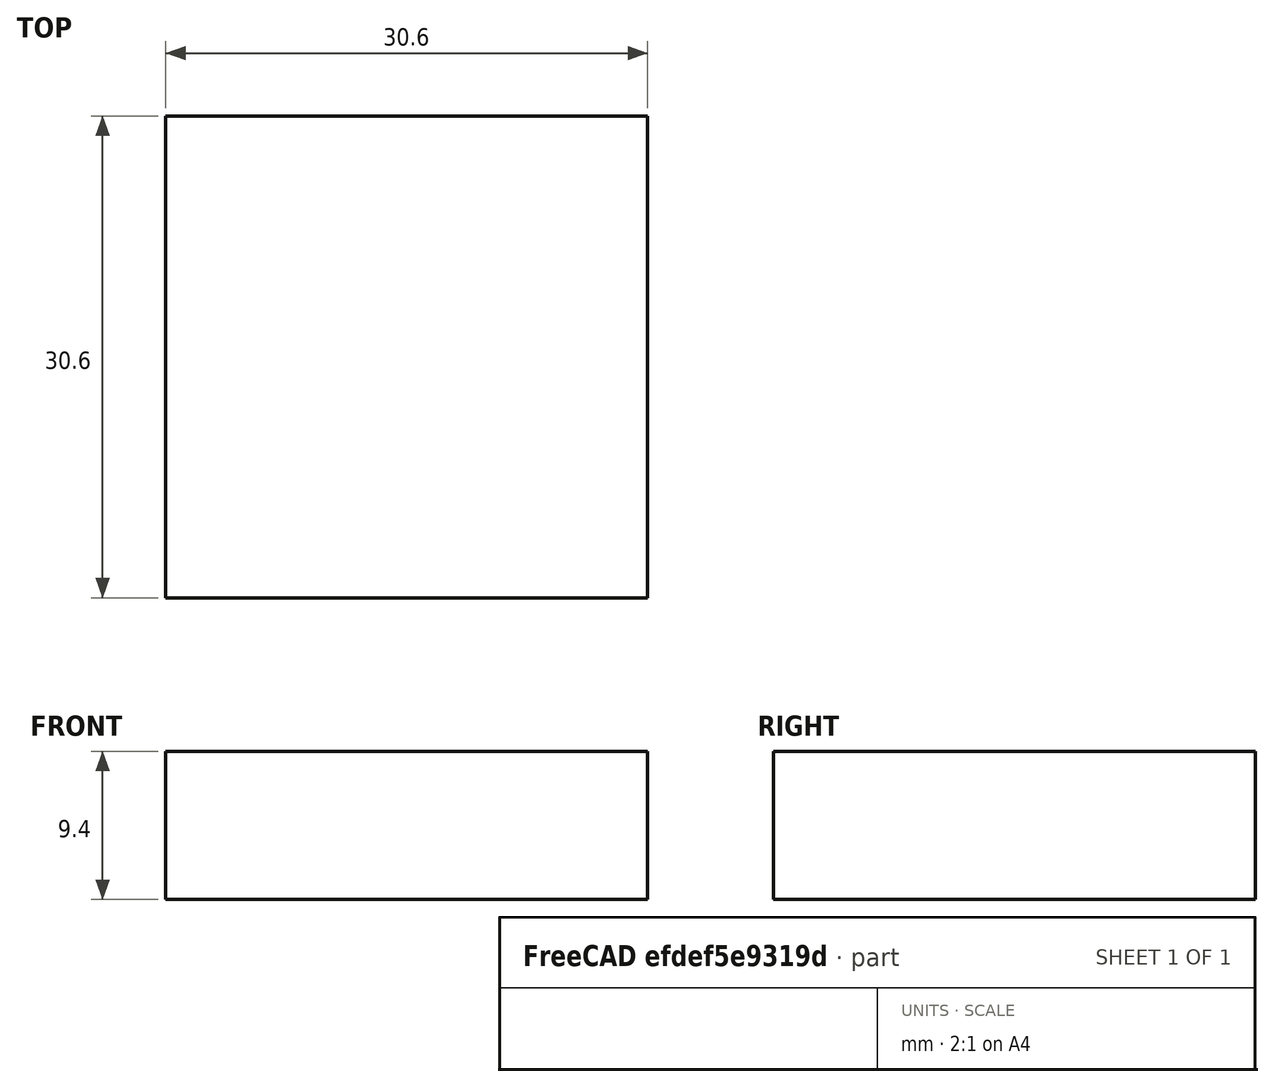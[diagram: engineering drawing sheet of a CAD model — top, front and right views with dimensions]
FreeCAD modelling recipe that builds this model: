
FCSTD DOCUMENT  (FreeCAD 0.17R13320 (Git))
Label: ring
License: All rights reserved
LicenseURL: http://en.wikipedia.org/wiki/All_rights_reserved
objects: Path::FeaturePython×7, Part::FeaturePython×2, Mesh::FeaturePython×2, Sketcher::SketchObject×1, PartDesign::Pad×1, PartDesign::Body×1, App::FeaturePython×1, Path::FeatureCompoundPython×1
note: 8 computed .brp shape members not serialized (recipe doc carries the construction recipe); baked Part::Feature solids carry a one-line shape summary decoded from their .brp

FEATURE [Sketcher::SketchObject] Sketch
  MapMode = 5
  Support = -> [XY_Plane]
  sketch-geometry (2):
    g0: Circle CenterX=0 CenterY=0 CenterZ=0 NormalX=0 NormalY=0 NormalZ=1 AngleXU=0 Radius=4.1
    g1: Circle CenterX=0 CenterY=0 CenterZ=0 NormalX=0 NormalY=0 NormalZ=1 AngleXU=0 Radius=4.9
  constraints (4):
    c: Coincident(g0,g-1)
    c: Coincident(g1,g-1)
    c: Radius(g0) = 4.1
    c: Radius(g1) = 4.9
FEATURE [PartDesign::Pad] Pad
  Length = 7
  Length2 = 100
  Profile = -> Sketch
  Type = 0
FEATURE [PartDesign::Body] Body
  Group = -> [Sketch,Pad]
  Origin = -> Origin
  Tip = -> Pad
FEATURE [App::FeaturePython] SetupSheet  # Path/CAM operation (typed FeaturePython)
  ClearanceHeightExpression = StartDepth+SetupSheet.ClearanceHeightOffset
  ClearanceHeightOffset = 5
  FinalDepthExpression = OpFinalDepth
  HorizRapid = 0
  SafeHeightExpression = StartDepth+SetupSheet.SafeHeightOffset
  SafeHeightOffset = 3
  StartDepthExpression = OpStartDepth
  StepDownExpression = OpToolDiameter
  VertRapid = 0
FEATURE [Part::FeaturePython] Clone  label="Base-Body"  # Draft clone (typed FeaturePython)
  AttacherType = Attacher::AttachEngine3D
  Fuse = false
  Objects = -> [Body]
  PathResource = Base
  Placement = pos=(14.9,14.9,-9.4) rot=(0,0,1;0rad)
  Scale = (1,1,1)
FEATURE [Path::FeaturePython] Default_Tool  label="Default Tool"  # Path/CAM operation (typed FeaturePython)
  HorizFeed = 0
  HorizRapid = 0
  SpindleDir = 0
  SpindleSpeed = 0
  ToolNumber = 1
  VertFeed = 0
  VertRapid = 0
  expr: HorizRapid = SetupSheet.HorizRapid
  expr: VertRapid = SetupSheet.VertRapid
FEATURE [Part::FeaturePython] Stock  # WARN: FeaturePython — macro-defined, semantics opaque (R4)
  Base = -> Body
  ExtXneg = 10
  ExtXpos = 10
  ExtYneg = 10
  ExtYpos = 10
  ExtZneg = 0
  ExtZpos = 2.4
  Placement = pos=(14.9,14.9,-9.4) rot=(0,0,1;0rad)
  StockType = FromBase
FEATURE [Path::FeaturePython] T3__8mm  label="T3: 8mm"  # Path/CAM operation (typed FeaturePython)
  HorizFeed = 0
  HorizRapid = 0
  SpindleDir = 0
  SpindleSpeed = 0
  ToolNumber = 3
  VertFeed = 0
  VertRapid = 0
  expr: HorizRapid = SetupSheet.HorizRapid
  expr: VertRapid = SetupSheet.VertRapid
FEATURE [Path::FeaturePython] Helix  # Path/CAM operation (typed FeaturePython)
  Active = true
  Base = -> [Clone]
  ClearanceHeight = 5
  Direction = 0
  FinalDepth = -10
  OpFinalDepth = -9.4
  OpStartDepth = 0
  OpToolDiameter = 8
  SafeHeight = 3
  StartDepth = 0
  StartSide = 0
  StepDown = 0.5
  StepOver = 30
  ToolController = -> T3__8mm
  expr: ClearanceHeight = StartDepth + SetupSheet.ClearanceHeightOffset
  expr: SafeHeight = StartDepth + SetupSheet.SafeHeightOffset
  expr: StartDepth = OpStartDepth
FEATURE [Path::FeaturePython] Contour  # Path/CAM operation (typed FeaturePython)
  Active = true
  AreaParams:
    OpenMode = 0
    Angle = 45.0
    MinArcPoints = 4
    Coplanar = 2
    Tolerance = 1e-07
    CleanDistance = 0.0
    PocketExtraOffset = 0.0
    RoundPrecision = 0.0
    AngleShift = 0.0
    SubjectFill = 0
    PocketMode = 0
    Simplify = False
    SectionTolerance = 1e-06
    MaxArcPoints = 100
    Offset = 4.0
    Accuracy = 0.01
    PocketStepover = 0.0
    ClipFill = 0
    ToolRadius = 1.0
    Outline = False
    ClipperScale = 10000000.0
    FromCenter = False
    Explode = False
    EndType = 0
    Shift = 0.0
    ExtraPass = 0
    Project = False
    JoinType = 0
    Thicken = False
    Stepdown = 1.0
    SectionMode = 2
    MiterLimit = 2.0
    Deflection = 0.01
    Reorient = True
    FitArcs = True
    SectionCount = -1
    SectionOffset = 0.0
    Stepover = 0.0
    Unit = 1.0
    Fill = 0
  ClearanceHeight = 5
  Direction = 0
  FinalDepth = -9.8
  JoinType = 0
  MiterLimit = 0.1
  OffsetExtra = 0
  OpFinalDepth = -9.4
  OpStartDepth = 0
  OpToolDiameter = 8
  PathParams = {'resume_height': 3.0, 'feedrate': 0.0, 'verbose': True, 'orientation': 1, 'return_end': True, 'preamble': False, 'retraction': 5.0, 'feedrate_v': 0.0}
  SafeHeight = 3
  Side = 0
  StartDepth = 0
  StartPoint = (0,0,0)
  StepDown = 0.5
  ToolController = -> T3__8mm
  UseComp = true
  UseStartPoint = false
  expr: ClearanceHeight = StartDepth + SetupSheet.ClearanceHeightOffset
  expr: SafeHeight = StartDepth + SetupSheet.SafeHeightOffset
  expr: StartDepth = OpStartDepth
FEATURE [Path::FeaturePython] MillFace  # Path/CAM operation (typed FeaturePython)
  Active = true
  AreaParams:
    OpenMode = 0
    Angle = 45.0
    MinArcPoints = 4
    Coplanar = 0
    Tolerance = 1e-07
    CleanDistance = 0.0
    PocketExtraOffset = -1.0
    RoundPrecision = 0.0
    AngleShift = 0.0
    SubjectFill = 0
    PocketMode = 2
    Simplify = False
    SectionTolerance = 1e-06
    MaxArcPoints = 100
    Offset = 0.0
    Accuracy = 0.01
    PocketStepover = 2.4
    ClipFill = 0
    ToolRadius = 4.0
    Outline = False
    ClipperScale = 10000000.0
    FromCenter = True
    Explode = False
    EndType = 0
    Shift = 0.0
    ExtraPass = 0
    Project = False
    JoinType = 0
    Thicken = False
    Stepdown = 1.0
    SectionMode = 2
    MiterLimit = 2.0
    Deflection = 0.01
    Reorient = True
    FitArcs = True
    SectionCount = -1
    SectionOffset = 0.0
    Stepover = 0.0
    Unit = 1.0
    Fill = 0
  Base = -> [Clone]
  BoundaryShape = 0
  ClearanceHeight = 5
  CutMode = 0
  ExtraOffset = 1
  FinalDepth = -2.4
  FinishDepth = 0
  KeepToolDown = false
  MinTravel = false
  OffsetPattern = 1
  OpFinalDepth = -2.4
  OpStartDepth = 0
  OpToolDiameter = 8
  PathParams = {'resume_height': 3.0, 'feedrate': 0.0, 'verbose': True, 'orientation': 1, 'return_end': True, 'preamble': False, 'retraction': 5.0, 'feedrate_v': 0.0}
  SafeHeight = 3
  StartAt = 0
  StartDepth = 0
  StartPoint = (0,0,0)
  StepDown = 0.5
  StepOver = 30
  ToolController = -> T3__8mm
  UseStartPoint = false
  ZigZagAngle = 45
  expr: ClearanceHeight = StartDepth + SetupSheet.ClearanceHeightOffset
  expr: SafeHeight = StartDepth + SetupSheet.SafeHeightOffset
  expr: FinalDepth = OpFinalDepth
  expr: StartDepth = OpStartDepth
FEATURE [Mesh::FeaturePython] CutMaterial  # WARN: FeaturePython — macro-defined, semantics opaque (R4)
FEATURE [Path::FeaturePython] TagDressup  # Path/CAM operation (typed FeaturePython)
  Angle = 45
  Base = -> Contour
  Disabled = [1]
  Height = 2
  Positions = (4) [(23.5838,16.8313,-9.8),(20.3299,7.8534,-9.8),(9.20031,8.06977,-9.8),(8.06977,20.5997,-9.8)]
  Radius = 0
  SegmentationFactor = 50
  Width = 3.1
FEATURE [Path::FeatureCompoundPython] Operations  # Path/CAM operation (typed FeaturePython)
  Group = -> [MillFace,Helix,TagDressup]
  UsePlacements = false
FEATURE [Path::FeaturePython] Job  # Path/CAM operation (typed FeaturePython)
  Base = -> Clone
  GeometryTolerance = 0.01
  Operations = -> Operations
  PostProcessor = 5
  SetupSheet = -> SetupSheet
  Stock = -> Stock
  ToolController = -> [Default_Tool,T3__8mm]
FEATURE [Mesh::FeaturePython] CutMaterial001  # WARN: FeaturePython — macro-defined, semantics opaque (R4)
